# Revit family: Dallmeier_Panomera_S-Series_Stadium
name_source: partatom
category: Sicherheitsgeräte
units: mm (PartAtom-declared; Revit-internal decimal feet)

## family parameters
Basisbauteil = Fläche
Beim Laden mit Abzugskörper schneiden = Nein
Bemaßung runder Anschluss = Durchmesser verwenden
Beschriftungsausrichtung beibehalten = Nein
Gemeinsam genutzt = Nein
Raumberechnungspunkt = Nein
Teiletyp = Normal

## types (14) — shared parameters
Hersteller = Dallmeier electronic GmbH
URL = https://www.dallmeier.com
Vorgabe-Ansicht = 121,9 cm
dimensions = 348x183x441mm
operating temperature = -40°C to +60°C
recommended network bandwidth = 1000 Mbps
voltage supply = 48 V

## per-type parameters (varying)
| type | FOV horizontal | FOV vertical | Modell | Modul_FOV_Horizontal | Pixel horizontal | aspect ratio | installation height | number of sensors | power consumption | required network bandwidth | weight |
| Panomera S8 Ultraline 66/61 | 61,00° | 16,00° | Panomera S4 Ultraline 66/61 | 9,68° | 2160 | 4:1 | 4.5 m to 10 m | 8 | 100 W | 128 Mbps | 17,50 kg |
| Panomera S8 Ultraline 66/45 | 45,00° | 11,70° | Panomera S4 Ultraline 66/45 | 7,07° | 2160 | 4:1 | 4.5 m to 9 m | 8 | 100 W | 128 Mbps | 17,50 kg |
| Panomera S8 Ultraline 66/41 | 41,20° | 24,50° | Panomera S4 Ultraline 66/41 | 11,15° | 2488 | 5:3 | 4.5 m to 10 m | 8 | 100 W | 128 Mbps | 17,50 kg |
| Panomera S8 Ultraline 66/30 | 30,00° | 7,80° | Panomera S4 Ultraline 66/30 | 4,68° | 2160 | 4:1 | 4.5 m to 9.5 m | 8 | 100 W | 128 Mbps | 17,50 kg |
| Panomera S8 Ultraline 66/29 | 29,30° | 17,40° | Panomera S4 Ultraline 66/29 | 8,14° | 2488 | 5:3 | 4.5 m to 10 m | 8 | 100 W | 128 Mbps | 17,50 kg |
| Panomera S8 Ultraline 66/20 | 20,20° | 12,10° | Panomera S4 Ultraline 66/20 | 5,39° | 2488 | 5:3 | 4.5 m to 9 m | 8 | 100 W | 128 Mbps | 17,50 kg |
| Panomera S8 Ultraline 66/13 | 13,00° | 7,80° | Panomera S4 Ultraline66/13 | 3,50° | 2488 | 5:3 | 4.5 m to 9 m | 8 | 100 W | 128 Mbps | 17,50 kg |
| Panomera S4 Ultraline 33/41 | 41,20° | 11,00° | Panomera S4 Ultraline 33/41 | 14,84° | 3312 | 15:4 | 4.5 m to 10 m | 4 | 70 W | 64 Mbps | 16,00 kg |
| Panomera S4 Ultraline 33/29 | 29,30° | 7,80° | Panomera S4 Ultraline 33/29 | 10,84° | 3312 | 15:4 | 4.5 m to 9 m | 4 | 70 W | 64 Mbps | 16,00 kg |
| Panomera S4 Ultraline 33/27 | 27,00° | 19,00° | Panomera S4 Ultraline 33/27 | 9,68° | 2160 | 5:3 | 4.5 m to 10 m | 4 | 70 W | 64 Mbps | 16,00 kg |
| Panomera S4 Ultraline 33/20 | 20,20° | 5,40° | Panomera S4 Ultraline 33/20 | 7,17° | 3312 | 15:4 | 4.5 m to 9.5 m | 4 | 70 W | 64 Mbps | 16,00 kg |
| Panomera S4 Ultraline 33/19 | 19,70° | 11,70° | Panomera S4 Ultraline 33/19 | 7,07° | 2160 | 5:3 | 4.5 m to 10 m | 4 | 70 W | 64 Mbps | 16,00 kg |
| Panomera S4 Ultraline 33/13 | 13,10° | 7,80° | Panomera S4 Ultraline 33/13 | 4,68° | 2160 | 5:3 | 4.5 m to 9 m | 4 | 70 W | 64 Mbps | 16,00 kg |
| Panomera S4 Ultraline 33/12 | 13,00° | 3,50° | Panomera S4 Ultraline 33/12 | 4,66° | 3312 | 15:4 | 4.5 m to 9 m | 4 | 70 W | 64 Mbps | 16,00 kg |

## geometry (parser evidence)
native form markers: Sweep x29
no freeform markers — native parametric forms only
